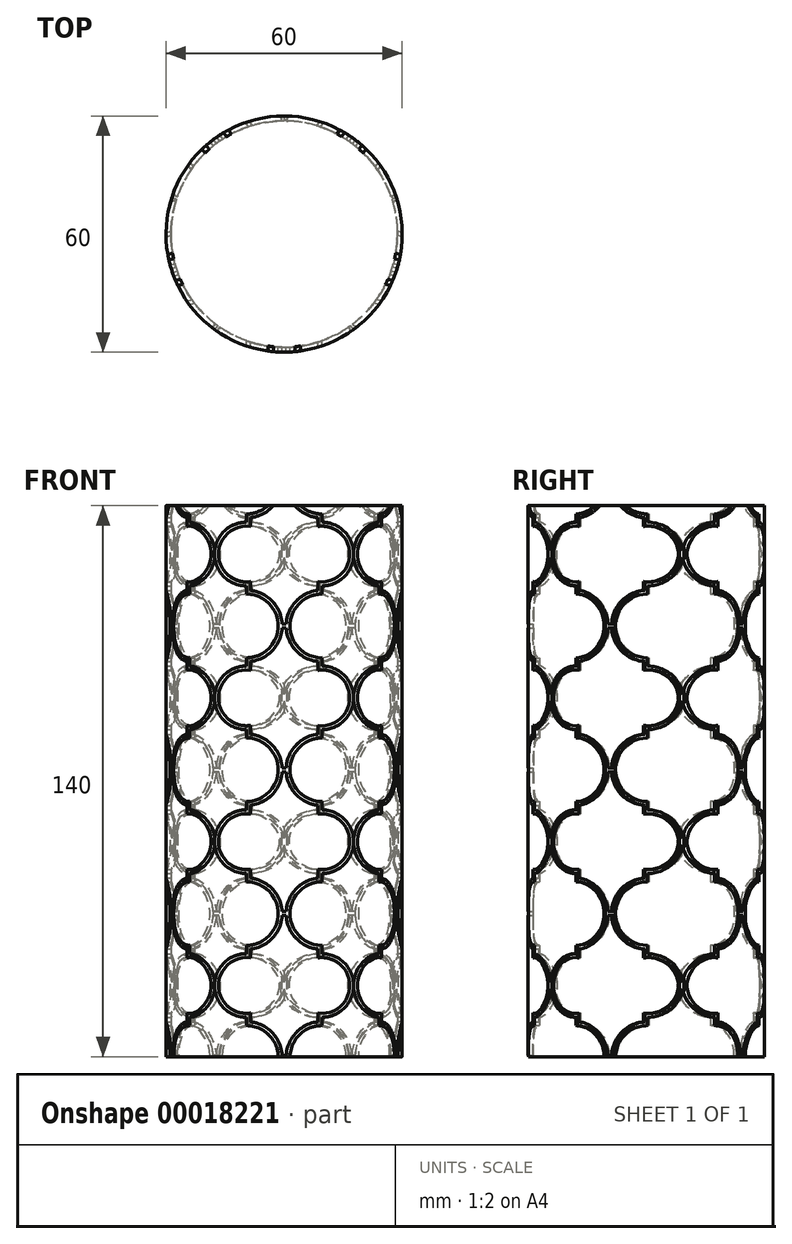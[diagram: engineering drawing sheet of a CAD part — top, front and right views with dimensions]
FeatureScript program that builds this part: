
annotation { "Feature Type Name" : "Feature", "Feature Type Description" : "" }
export const myFeature = defineFeature(function(context is Context, id is Id, definition is map)
    precondition{}
    {
        {
            var Q0;
            Q0=qCreatedBy(makeId("Top.planeOp"),FACE);
            var sketch = newSketch(context, id + "F0", { "sketchPlane" : qUnion([Q0])});
            skCircle(sketch, "E0", {"center": v(0, 0) * mm, "radius": 30 * mm});
            skCircle(sketch, "E1", {"center": v(0, 0) * mm, "radius": 28.75 * mm});
            skSolve(sketch);
        }
        {
            var Q0;
            Q0=makeQuery(id+"F0.imprint","IMPRINT",FACE,{"disambiguationData":[TD([[makeQuery(id+"F0.imprint","IMPRINT",EDGE,{"derivedFrom":sQuery(id+"F0.wireOp",EDGE,"E0")}),1.0]])]});
            extrude(context, id + "F1", {"entities" : qUnion([Q0]), "depth" : 140 * mm});
        }
        {
            var Q0;
            Q0=qCreatedBy(makeId("Front.planeOp"),FACE);
            var sketch = newSketch(context, id + "F2", { "sketchPlane" : qUnion([Q0])});
            skLineSegment(sketch, "E2", {"start": v(0, 0) * mm, "end": v(-17.68, 18.08) * mm, "construction": true});
            skLineSegment(sketch, "E3", {"start": v(-17.68, 18.08) * mm, "end": v(0, 36.36) * mm, "construction": true});
            skLineSegment(sketch, "E4", {"start": v(0, 36.35) * mm, "end": v(17.68, 18.08) * mm, "construction": true});
            skLineSegment(sketch, "E5", {"start": v(17.68, 18.08) * mm, "end": v(0, 0) * mm, "construction": true});
            skArc(sketch, "E6", {"start": v(-9.59, 26.17) * mm, "mid": v(-17.68, 18.08) * mm, "end": v(-9.59, 10) * mm});
            skArc(sketch, "E7", {"start": v(9.59, 10) * mm, "mid": v(17.68, 18.08) * mm, "end": v(9.59, 26.17) * mm});
            skLineSegment(sketch, "E8", {"start": v(-17.68, 18.08) * mm, "end": v(17.68, 18.08) * mm, "construction": true});
            skLineSegment(sketch, "E9", {"start": v(-9.59, 26.17) * mm, "end": v(-9.59, 28.27) * mm});
            skLineSegment(sketch, "E10", {"start": v(9.59, 26.17) * mm, "end": v(9.59, 28.27) * mm});
            skLineSegment(sketch, "E11", {"start": v(-1.5, 36.35) * mm, "end": v(1.5, 36.35) * mm, "construction": true});
            skArc(sketch, "E12", {"start": v(-9.59, 28.27) * mm, "mid": v(-3.87, 30.64) * mm, "end": v(-1.5, 36.35) * mm});
            skArc(sketch, "E13", {"start": v(1.5, 36.35) * mm, "mid": v(3.87, 30.64) * mm, "end": v(9.59, 28.27) * mm});
            skPoint(sketch, "E14", {"position": v(0, 36.35) * mm});
            skLineSegment(sketch, "E15.MirrorCS", {"start": v(-9.59, 10) * mm, "end": v(-9.59, 7.9) * mm});
            skLineSegment(sketch, "E16.MirrorCS", {"start": v(9.59, 10) * mm, "end": v(9.59, 7.9) * mm});
            skArc(sketch, "E17.MirrorCS", {"start": v(1.5, -0.19) * mm, "mid": v(3.87, 5.53) * mm, "end": v(9.59, 7.9) * mm});
            skArc(sketch, "E18.MirrorCS", {"start": v(-9.59, 7.9) * mm, "mid": v(-3.87, 5.53) * mm, "end": v(-1.5, -0.19) * mm});
            skPoint(sketch, "E19", {"position": v(0, 18.08) * mm});
            skCircle(sketch, "E20", {"center": v(0, 18.08) * mm, "radius": 12.54 * mm, "construction": true});
            skLineSegment(sketch, "E21", {"start": v(-1.5, -0.19) * mm, "end": v(1.5, -0.19) * mm});
            skArc(sketch, "E22.0", {"start": v(-8.59, 27.32) * mm, "mid": v(-2.99, 30.1) * mm, "end": v(-0.51, 35.85) * mm});
            skLineSegment(sketch, "E22.1", {"start": v(-8.59, 25.1) * mm, "end": v(-8.59, 27.32) * mm});
            skArc(sketch, "E22.2", {"start": v(-8.59, 25.1) * mm, "mid": v(-16.68, 18.08) * mm, "end": v(-8.59, 11.07) * mm});
            skLineSegment(sketch, "E22.3", {"start": v(-8.59, 11.07) * mm, "end": v(-8.59, 8.85) * mm});
            skArc(sketch, "E22.4", {"start": v(-8.59, 8.85) * mm, "mid": v(-2.99, 6.06) * mm, "end": v(-0.51, 0.31) * mm});
            skArc(sketch, "E23.0", {"start": v(0.51, 35.85) * mm, "mid": v(2.99, 30.1) * mm, "end": v(8.59, 27.32) * mm});
            skLineSegment(sketch, "E23.1", {"start": v(8.59, 25.1) * mm, "end": v(8.59, 27.32) * mm});
            skArc(sketch, "E23.2", {"start": v(8.59, 11.07) * mm, "mid": v(16.68, 18.08) * mm, "end": v(8.59, 25.1) * mm});
            skLineSegment(sketch, "E23.3", {"start": v(8.59, 11.07) * mm, "end": v(8.59, 8.85) * mm});
            skArc(sketch, "E23.4", {"start": v(0.51, 0.31) * mm, "mid": v(2.99, 6.06) * mm, "end": v(8.59, 8.85) * mm});
            skLineSegment(sketch, "E24.0", {"start": v(-0.51, 35.85) * mm, "end": v(0.51, 35.85) * mm});
            skLineSegment(sketch, "E25.0", {"start": v(-0.51, 0.31) * mm, "end": v(0.51, 0.31) * mm});
            skPoint(sketch, "E26.end.orphan", {"position": v(-9.59, 44.44) * mm});
            skPoint(sketch, "E27.start.orphan", {"position": v(9.59, 44.44) * mm});
            skLineSegment(sketch, "E28", {"start": v(0, 0) * mm, "end": v(0, 140) * mm, "construction": true});
            skArc(sketch, "E29.0.1.5", {"start": v(-9.59, 64.8) * mm, "mid": v(-3.87, 67.18) * mm, "end": v(-1.5, 72.9) * mm});
            skLineSegment(sketch, "E29.0.1.9", {"start": v(-17.68, 54.63) * mm, "end": v(0, 72.9) * mm, "construction": true});
            skLineSegment(sketch, "E29.0.1.10", {"start": v(0, 36.54) * mm, "end": v(-17.68, 54.63) * mm, "construction": true});
            skLineSegment(sketch, "E29.0.1.13", {"start": v(-17.68, 54.63) * mm, "end": v(17.68, 54.63) * mm, "construction": true});
            skLineSegment(sketch, "E29.0.1.19", {"start": v(0, 72.9) * mm, "end": v(17.68, 54.63) * mm, "construction": true});
            skArc(sketch, "E29.0.1.24", {"start": v(-9.59, 62.71) * mm, "mid": v(-17.68, 54.63) * mm, "end": v(-9.59, 46.54) * mm});
            skArc(sketch, "E29.0.1.25", {"start": v(-9.59, 44.44) * mm, "mid": v(-3.87, 42.07) * mm, "end": v(-1.5, 36.35) * mm});
            skArc(sketch, "E29.0.1.27", {"start": v(1.5, 36.35) * mm, "mid": v(3.87, 42.07) * mm, "end": v(9.59, 44.44) * mm});
            skLineSegment(sketch, "E29.0.1.28", {"start": v(17.68, 54.63) * mm, "end": v(0, 36.54) * mm, "construction": true});
            skLineSegment(sketch, "E29.0.1.29", {"start": v(-9.59, 62.71) * mm, "end": v(-9.59, 64.8) * mm});
            skArc(sketch, "E29.0.1.33", {"start": v(9.59, 46.54) * mm, "mid": v(17.68, 54.63) * mm, "end": v(9.59, 62.71) * mm});
            skLineSegment(sketch, "E29.0.1.36", {"start": v(9.59, 62.71) * mm, "end": v(9.59, 64.8) * mm});
            skPoint(sketch, "E29.0.1.38", {"position": v(9.59, 80.98) * mm});
            skPoint(sketch, "E29.0.1.41", {"position": v(0, 54.63) * mm});
            skArc(sketch, "E29.0.1.44", {"start": v(-8.59, 45.39) * mm, "mid": v(-2.99, 42.6) * mm, "end": v(-0.51, 36.85) * mm});
            skArc(sketch, "E29.0.1.47", {"start": v(8.59, 47.6) * mm, "mid": v(16.68, 54.63) * mm, "end": v(8.59, 61.64) * mm});
            skPoint(sketch, "E29.0.1.48", {"position": v(0, 72.9) * mm});
            skArc(sketch, "E29.0.1.49", {"start": v(1.5, 72.9) * mm, "mid": v(3.87, 67.18) * mm, "end": v(9.59, 64.8) * mm});
            skArc(sketch, "E29.0.1.54", {"start": v(0.51, 72.4) * mm, "mid": v(2.99, 66.65) * mm, "end": v(8.59, 63.86) * mm});
            skCircle(sketch, "E29.0.1.58", {"center": v(0, 54.63) * mm, "radius": 12.54 * mm, "construction": true});
            skPoint(sketch, "E29.0.1.61", {"position": v(-9.59, 80.98) * mm});
            skArc(sketch, "E29.0.1.63", {"start": v(-8.59, 61.64) * mm, "mid": v(-16.68, 54.63) * mm, "end": v(-8.59, 47.6) * mm});
            skLineSegment(sketch, "E29.0.1.70", {"start": v(-8.59, 47.6) * mm, "end": v(-8.59, 45.39) * mm});
            skLineSegment(sketch, "E29.0.1.76", {"start": v(-8.59, 61.64) * mm, "end": v(-8.59, 63.86) * mm});
            skArc(sketch, "E29.0.1.87", {"start": v(-8.59, 63.86) * mm, "mid": v(-2.99, 66.65) * mm, "end": v(-0.51, 72.4) * mm});
            skArc(sketch, "E29.0.1.89", {"start": v(0.51, 36.85) * mm, "mid": v(2.99, 42.6) * mm, "end": v(8.59, 45.39) * mm});
            skLineSegment(sketch, "E29.0.1.95", {"start": v(9.59, 46.54) * mm, "end": v(9.59, 44.44) * mm});
            skLineSegment(sketch, "E29.0.1.96", {"start": v(8.59, 47.6) * mm, "end": v(8.59, 45.39) * mm});
            skLineSegment(sketch, "E29.0.1.99", {"start": v(-1.5, 72.9) * mm, "end": v(1.5, 72.9) * mm});
            skLineSegment(sketch, "E29.0.1.100", {"start": v(8.59, 61.64) * mm, "end": v(8.59, 63.86) * mm});
            skLineSegment(sketch, "E29.0.1.102", {"start": v(-9.59, 46.54) * mm, "end": v(-9.59, 44.44) * mm});
            skLineSegment(sketch, "E29.0.1.103", {"start": v(-0.51, 72.4) * mm, "end": v(0.51, 72.4) * mm});
            skLineSegment(sketch, "E29.0.1.104", {"start": v(-0.51, 36.85) * mm, "end": v(0.51, 36.85) * mm});
            skArc(sketch, "E29.0.2.5", {"start": v(-9.59, 101.35) * mm, "mid": v(-3.87, 103.72) * mm, "end": v(-1.5, 109.44) * mm});
            skLineSegment(sketch, "E29.0.2.9", {"start": v(-17.68, 91.17) * mm, "end": v(0, 109.44) * mm, "construction": true});
            skLineSegment(sketch, "E29.0.2.10", {"start": v(0, 73.08) * mm, "end": v(-17.68, 91.17) * mm, "construction": true});
            skLineSegment(sketch, "E29.0.2.13", {"start": v(-17.68, 91.17) * mm, "end": v(17.68, 91.17) * mm, "construction": true});
            skLineSegment(sketch, "E29.0.2.19", {"start": v(0, 109.44) * mm, "end": v(17.68, 91.17) * mm, "construction": true});
            skArc(sketch, "E29.0.2.24", {"start": v(-9.59, 99.25) * mm, "mid": v(-17.68, 91.17) * mm, "end": v(-9.59, 83.08) * mm});
            skArc(sketch, "E29.0.2.25", {"start": v(-9.59, 80.98) * mm, "mid": v(-3.87, 78.62) * mm, "end": v(-1.5, 72.9) * mm});
            skArc(sketch, "E29.0.2.27", {"start": v(1.5, 72.9) * mm, "mid": v(3.87, 78.62) * mm, "end": v(9.59, 80.98) * mm});
            skLineSegment(sketch, "E29.0.2.28", {"start": v(17.68, 91.17) * mm, "end": v(0, 73.08) * mm, "construction": true});
            skLineSegment(sketch, "E29.0.2.29", {"start": v(-9.59, 99.25) * mm, "end": v(-9.59, 101.35) * mm});
            skLineSegment(sketch, "E29.0.2.32", {"start": v(-1.5, 72.9) * mm, "end": v(1.5, 72.9) * mm});
            skArc(sketch, "E29.0.2.33", {"start": v(9.59, 83.08) * mm, "mid": v(17.68, 91.17) * mm, "end": v(9.59, 99.25) * mm});
            skLineSegment(sketch, "E29.0.2.36", {"start": v(9.59, 99.25) * mm, "end": v(9.59, 101.35) * mm});
            skPoint(sketch, "E29.0.2.38", {"position": v(9.59, 117.53) * mm});
            skPoint(sketch, "E29.0.2.41", {"position": v(0, 91.17) * mm});
            skArc(sketch, "E29.0.2.44", {"start": v(-8.59, 81.93) * mm, "mid": v(-2.99, 79.14) * mm, "end": v(-0.51, 73.4) * mm});
            skArc(sketch, "E29.0.2.47", {"start": v(8.59, 84.15) * mm, "mid": v(16.68, 91.17) * mm, "end": v(8.59, 98.18) * mm});
            skPoint(sketch, "E29.0.2.48", {"position": v(0, 109.44) * mm});
            skArc(sketch, "E29.0.2.49", {"start": v(1.5, 109.44) * mm, "mid": v(3.87, 103.72) * mm, "end": v(9.59, 101.35) * mm});
            skArc(sketch, "E29.0.2.54", {"start": v(0.51, 108.94) * mm, "mid": v(2.99, 103.19) * mm, "end": v(8.59, 100.4) * mm});
            skCircle(sketch, "E29.0.2.58", {"center": v(0, 91.17) * mm, "radius": 12.54 * mm, "construction": true});
            skPoint(sketch, "E29.0.2.61", {"position": v(-9.59, 117.53) * mm});
            skArc(sketch, "E29.0.2.63", {"start": v(-8.59, 98.18) * mm, "mid": v(-16.68, 91.17) * mm, "end": v(-8.59, 84.15) * mm});
            skLineSegment(sketch, "E29.0.2.70", {"start": v(-8.59, 84.15) * mm, "end": v(-8.59, 81.93) * mm});
            skLineSegment(sketch, "E29.0.2.76", {"start": v(-8.59, 98.18) * mm, "end": v(-8.59, 100.4) * mm});
            skArc(sketch, "E29.0.2.87", {"start": v(-8.59, 100.4) * mm, "mid": v(-2.99, 103.19) * mm, "end": v(-0.51, 108.94) * mm});
            skArc(sketch, "E29.0.2.89", {"start": v(0.51, 73.4) * mm, "mid": v(2.99, 79.14) * mm, "end": v(8.59, 81.93) * mm});
            skLineSegment(sketch, "E29.0.2.95", {"start": v(9.59, 83.08) * mm, "end": v(9.59, 80.98) * mm});
            skLineSegment(sketch, "E29.0.2.96", {"start": v(8.59, 84.15) * mm, "end": v(8.59, 81.93) * mm});
            skLineSegment(sketch, "E29.0.2.99", {"start": v(-1.5, 109.44) * mm, "end": v(1.5, 109.44) * mm});
            skLineSegment(sketch, "E29.0.2.100", {"start": v(8.59, 98.18) * mm, "end": v(8.59, 100.4) * mm});
            skLineSegment(sketch, "E29.0.2.102", {"start": v(-9.59, 83.08) * mm, "end": v(-9.59, 80.98) * mm});
            skLineSegment(sketch, "E29.0.2.103", {"start": v(-0.51, 108.94) * mm, "end": v(0.51, 108.94) * mm});
            skLineSegment(sketch, "E29.0.2.104", {"start": v(-0.51, 73.4) * mm, "end": v(0.51, 73.4) * mm});
            skArc(sketch, "E29.0.3.5", {"start": v(-9.59, 137.89) * mm, "mid": v(-3.87, 140.26) * mm, "end": v(-1.5, 145.98) * mm});
            skLineSegment(sketch, "E29.0.3.9", {"start": v(-17.68, 127.7) * mm, "end": v(0, 145.98) * mm, "construction": true});
            skLineSegment(sketch, "E29.0.3.10", {"start": v(0, 109.62) * mm, "end": v(-17.68, 127.7) * mm, "construction": true});
            skLineSegment(sketch, "E29.0.3.13", {"start": v(-17.68, 127.7) * mm, "end": v(17.68, 127.7) * mm, "construction": true});
            skLineSegment(sketch, "E29.0.3.19", {"start": v(0, 145.98) * mm, "end": v(17.68, 127.7) * mm, "construction": true});
            skArc(sketch, "E29.0.3.24", {"start": v(-9.59, 135.8) * mm, "mid": v(-17.68, 127.7) * mm, "end": v(-9.59, 119.62) * mm});
            skArc(sketch, "E29.0.3.25", {"start": v(-9.59, 117.53) * mm, "mid": v(-3.87, 115.16) * mm, "end": v(-1.5, 109.44) * mm});
            skArc(sketch, "E29.0.3.27", {"start": v(1.5, 109.44) * mm, "mid": v(3.87, 115.16) * mm, "end": v(9.59, 117.53) * mm});
            skLineSegment(sketch, "E29.0.3.28", {"start": v(17.68, 127.7) * mm, "end": v(0, 109.62) * mm, "construction": true});
            skLineSegment(sketch, "E29.0.3.29", {"start": v(-9.59, 135.8) * mm, "end": v(-9.59, 137.89) * mm});
            skLineSegment(sketch, "E29.0.3.32", {"start": v(-1.5, 109.44) * mm, "end": v(1.5, 109.44) * mm});
            skArc(sketch, "E29.0.3.33", {"start": v(9.59, 119.62) * mm, "mid": v(17.68, 127.7) * mm, "end": v(9.59, 135.8) * mm});
            skLineSegment(sketch, "E29.0.3.36", {"start": v(9.59, 135.8) * mm, "end": v(9.59, 137.89) * mm});
            skPoint(sketch, "E29.0.3.38", {"position": v(9.59, 154.07) * mm});
            skPoint(sketch, "E29.0.3.41", {"position": v(0, 127.7) * mm});
            skArc(sketch, "E29.0.3.44", {"start": v(-8.59, 118.47) * mm, "mid": v(-2.99, 115.68) * mm, "end": v(-0.51, 109.94) * mm});
            skArc(sketch, "E29.0.3.47", {"start": v(8.59, 120.69) * mm, "mid": v(16.68, 127.7) * mm, "end": v(8.59, 134.72) * mm});
            skPoint(sketch, "E29.0.3.48", {"position": v(0, 145.98) * mm});
            skArc(sketch, "E29.0.3.49", {"start": v(1.5, 145.98) * mm, "mid": v(3.87, 140.26) * mm, "end": v(9.59, 137.89) * mm});
            skArc(sketch, "E29.0.3.54", {"start": v(0.51, 145.48) * mm, "mid": v(2.99, 139.73) * mm, "end": v(8.59, 136.94) * mm});
            skCircle(sketch, "E29.0.3.58", {"center": v(0, 127.7) * mm, "radius": 12.54 * mm, "construction": true});
            skPoint(sketch, "E29.0.3.61", {"position": v(-9.59, 154.07) * mm});
            skArc(sketch, "E29.0.3.63", {"start": v(-8.59, 134.72) * mm, "mid": v(-16.68, 127.7) * mm, "end": v(-8.59, 120.69) * mm});
            skLineSegment(sketch, "E29.0.3.70", {"start": v(-8.59, 120.69) * mm, "end": v(-8.59, 118.47) * mm});
            skLineSegment(sketch, "E29.0.3.76", {"start": v(-8.59, 134.72) * mm, "end": v(-8.59, 136.94) * mm});
            skArc(sketch, "E29.0.3.87", {"start": v(-8.59, 136.94) * mm, "mid": v(-2.99, 139.73) * mm, "end": v(-0.51, 145.48) * mm});
            skArc(sketch, "E29.0.3.89", {"start": v(0.51, 109.94) * mm, "mid": v(2.99, 115.68) * mm, "end": v(8.59, 118.47) * mm});
            skLineSegment(sketch, "E29.0.3.95", {"start": v(9.59, 119.62) * mm, "end": v(9.59, 117.53) * mm});
            skLineSegment(sketch, "E29.0.3.96", {"start": v(8.59, 120.69) * mm, "end": v(8.59, 118.47) * mm});
            skLineSegment(sketch, "E29.0.3.99", {"start": v(-1.5, 145.98) * mm, "end": v(1.5, 145.98) * mm});
            skLineSegment(sketch, "E29.0.3.100", {"start": v(8.59, 134.72) * mm, "end": v(8.59, 136.94) * mm});
            skLineSegment(sketch, "E29.0.3.102", {"start": v(-9.59, 119.62) * mm, "end": v(-9.59, 117.53) * mm});
            skLineSegment(sketch, "E29.0.3.103", {"start": v(-0.51, 145.48) * mm, "end": v(0.51, 145.48) * mm});
            skLineSegment(sketch, "E29.0.3.104", {"start": v(-0.51, 109.94) * mm, "end": v(0.51, 109.94) * mm});
            skLineSegment(sketch, "E29.direction1", {"start": v(-9.59, -0.19) * mm, "end": v(15.41, -0.19) * mm, "construction": true});
            skLineSegment(sketch, "E29.direction2", {"start": v(-9.59, -0.19) * mm, "end": v(-9.59, 36.35) * mm, "construction": true});
            skSolve(sketch);
        }
        {
            var Q0;
            Q0=makeQuery(id+"F2.imprint","IMPRINT",FACE,{"disambiguationData":[TD([[makeQuery(id+"F2.imprint","IMPRINT",EDGE,{"derivedFrom":sQuery(id+"F2.wireOp",EDGE,"E6")}),1.0]])]});
            var Q1;
            Q1=makeQuery(id+"F2.imprint","IMPRINT",FACE,{"disambiguationData":[TD([[makeQuery(id+"F2.imprint","IMPRINT",EDGE,{"derivedFrom":sQuery(id+"F2.wireOp",EDGE,"E29.0.2.5")}),-1.0]])]});
            var Q2;
            Q2=makeQuery(id+"F2.imprint","IMPRINT",FACE,{"disambiguationData":[TD([[makeQuery(id+"F2.imprint","IMPRINT",EDGE,{"derivedFrom":sQuery(id+"F2.wireOp",EDGE,"E29.0.3.5")}),-1.0]])]});
            var Q3;
            Q3=makeQuery(id+"F1.opExtrude","SWEPT_FACE",FACE,{"disambiguationData":[OSD([sQuery(id+"F0.wireOp",EDGE,"E0")])]});
            extrude(context, id + "F3", {"entities" : qUnion([Q0, Q1, Q2]), "endBound" : BoundingType.UP_TO_SURFACE, "endBoundEntityFace" : qUnion([Q3]), "depth" : 25 * mm});
        }
        {
            var Q0;
            Q0=makeQuery(id+"F3.opExtrude","SWEPT_BODY",BODY,{"disambiguationData":[OSD([sQuery(id+"F2.wireOp",EDGE,"E6"),sQuery(id+"F2.wireOp",EDGE,"E7"),sQuery(id+"F2.wireOp",EDGE,"E9"),sQuery(id+"F2.wireOp",EDGE,"E10"),sQuery(id+"F2.wireOp",EDGE,"E12"),sQuery(id+"F2.wireOp",EDGE,"E13"),sQuery(id+"F2.wireOp",EDGE,"E15.MirrorCS"),sQuery(id+"F2.wireOp",EDGE,"E16.MirrorCS"),sQuery(id+"F2.wireOp",EDGE,"E17.MirrorCS"),sQuery(id+"F2.wireOp",EDGE,"E18.MirrorCS"),sQuery(id+"F2.wireOp",EDGE,"E21"),sQuery(id+"F2.wireOp",EDGE,"E22.0"),sQuery(id+"F2.wireOp",EDGE,"E22.1"),sQuery(id+"F2.wireOp",EDGE,"E22.2"),sQuery(id+"F2.wireOp",EDGE,"E22.3"),sQuery(id+"F2.wireOp",EDGE,"E22.4"),sQuery(id+"F2.wireOp",EDGE,"E23.0"),sQuery(id+"F2.wireOp",EDGE,"E23.1"),sQuery(id+"F2.wireOp",EDGE,"E23.2"),sQuery(id+"F2.wireOp",EDGE,"E23.3"),sQuery(id+"F2.wireOp",EDGE,"E23.4"),sQuery(id+"F2.wireOp",EDGE,"E24.0"),sQuery(id+"F2.wireOp",EDGE,"E25.0"),sQuery(id+"F2.wireOp",EDGE,"E29.0.1.5"),sQuery(id+"F2.wireOp",EDGE,"E29.0.1.24"),sQuery(id+"F2.wireOp",EDGE,"E29.0.1.25"),sQuery(id+"F2.wireOp",EDGE,"E29.0.1.27"),sQuery(id+"F2.wireOp",EDGE,"E29.0.1.29"),sQuery(id+"F2.wireOp",EDGE,"E29.0.1.33"),sQuery(id+"F2.wireOp",EDGE,"E29.0.1.36"),sQuery(id+"F2.wireOp",EDGE,"E29.0.1.44"),sQuery(id+"F2.wireOp",EDGE,"E29.0.1.47"),sQuery(id+"F2.wireOp",EDGE,"E29.0.1.49"),sQuery(id+"F2.wireOp",EDGE,"E29.0.1.54"),sQuery(id+"F2.wireOp",EDGE,"E29.0.1.63"),sQuery(id+"F2.wireOp",EDGE,"E29.0.1.70"),sQuery(id+"F2.wireOp",EDGE,"E29.0.1.76"),sQuery(id+"F2.wireOp",EDGE,"E29.0.1.87"),sQuery(id+"F2.wireOp",EDGE,"E29.0.1.89"),sQuery(id+"F2.wireOp",EDGE,"E29.0.1.95"),sQuery(id+"F2.wireOp",EDGE,"E29.0.1.96"),sQuery(id+"F2.wireOp",EDGE,"E29.0.1.100"),sQuery(id+"F2.wireOp",EDGE,"E29.0.1.102"),sQuery(id+"F2.wireOp",EDGE,"E29.0.1.103"),sQuery(id+"F2.wireOp",EDGE,"E29.0.1.104"),sQuery(id+"F2.wireOp",EDGE,"E29.0.2.5"),sQuery(id+"F2.wireOp",EDGE,"E29.0.2.24"),sQuery(id+"F2.wireOp",EDGE,"E29.0.2.25"),sQuery(id+"F2.wireOp",EDGE,"E29.0.2.27"),sQuery(id+"F2.wireOp",EDGE,"E29.0.2.29"),sQuery(id+"F2.wireOp",EDGE,"E29.0.2.33"),sQuery(id+"F2.wireOp",EDGE,"E29.0.2.36"),sQuery(id+"F2.wireOp",EDGE,"E29.0.2.44"),sQuery(id+"F2.wireOp",EDGE,"E29.0.2.47"),sQuery(id+"F2.wireOp",EDGE,"E29.0.2.49"),sQuery(id+"F2.wireOp",EDGE,"E29.0.2.54"),sQuery(id+"F2.wireOp",EDGE,"E29.0.2.63"),sQuery(id+"F2.wireOp",EDGE,"E29.0.2.70"),sQuery(id+"F2.wireOp",EDGE,"E29.0.2.76"),sQuery(id+"F2.wireOp",EDGE,"E29.0.2.87"),sQuery(id+"F2.wireOp",EDGE,"E29.0.2.89"),sQuery(id+"F2.wireOp",EDGE,"E29.0.2.95"),sQuery(id+"F2.wireOp",EDGE,"E29.0.2.96"),sQuery(id+"F2.wireOp",EDGE,"E29.0.2.100"),sQuery(id+"F2.wireOp",EDGE,"E29.0.2.102"),sQuery(id+"F2.wireOp",EDGE,"E29.0.2.103"),sQuery(id+"F2.wireOp",EDGE,"E29.0.2.104"),sQuery(id+"F2.wireOp",EDGE,"E29.0.3.5"),sQuery(id+"F2.wireOp",EDGE,"E29.0.3.24"),sQuery(id+"F2.wireOp",EDGE,"E29.0.3.25"),sQuery(id+"F2.wireOp",EDGE,"E29.0.3.27"),sQuery(id+"F2.wireOp",EDGE,"E29.0.3.29"),sQuery(id+"F2.wireOp",EDGE,"E29.0.3.33"),sQuery(id+"F2.wireOp",EDGE,"E29.0.3.36"),sQuery(id+"F2.wireOp",EDGE,"E29.0.3.44"),sQuery(id+"F2.wireOp",EDGE,"E29.0.3.47"),sQuery(id+"F2.wireOp",EDGE,"E29.0.3.49"),sQuery(id+"F2.wireOp",EDGE,"E29.0.3.54"),sQuery(id+"F2.wireOp",EDGE,"E29.0.3.63"),sQuery(id+"F2.wireOp",EDGE,"E29.0.3.70"),sQuery(id+"F2.wireOp",EDGE,"E29.0.3.76"),sQuery(id+"F2.wireOp",EDGE,"E29.0.3.87"),sQuery(id+"F2.wireOp",EDGE,"E29.0.3.89"),sQuery(id+"F2.wireOp",EDGE,"E29.0.3.95"),sQuery(id+"F2.wireOp",EDGE,"E29.0.3.96"),sQuery(id+"F2.wireOp",EDGE,"E29.0.3.99"),sQuery(id+"F2.wireOp",EDGE,"E29.0.3.100"),sQuery(id+"F2.wireOp",EDGE,"E29.0.3.102"),sQuery(id+"F2.wireOp",EDGE,"E29.0.3.103"),sQuery(id+"F2.wireOp",EDGE,"E29.0.3.104")])]});
            var Q1;
            Q1=makeQuery(id+"F1.opExtrude","CAP_EDGE",EDGE,{"disambiguationData":[OSD([sQuery(id+"F0.wireOp",EDGE,"E0")])],"isStart":false});
            circularPattern(context, id + "F4", {"operationType" : NewBodyOperationType.REMOVE, "entities" : qUnion([Q0]), "axis" : qUnion([Q1]), "angle" : 360 * degree, "instanceCount" : 5, "equalSpace" : true});
        }
        {
            var Q0;
            Q0=qCreatedBy(makeId("Top.planeOp"),FACE);
            var sketch = newSketch(context, id + "F5", { "sketchPlane" : qUnion([Q0])});
            skCircle(sketch, "E30", {"center": v(0, 0) * mm, "radius": 28.75 * mm});
            skSolve(sketch);
        }
        {
            var Q0;
            Q0 = qSketchRegion(id + "F5", true);
            extrude(context, id + "F6", {"entities" : qUnion([Q0]), "operationType" : NewBodyOperationType.ADD, "depth" : 140 * mm});
        }
    });
